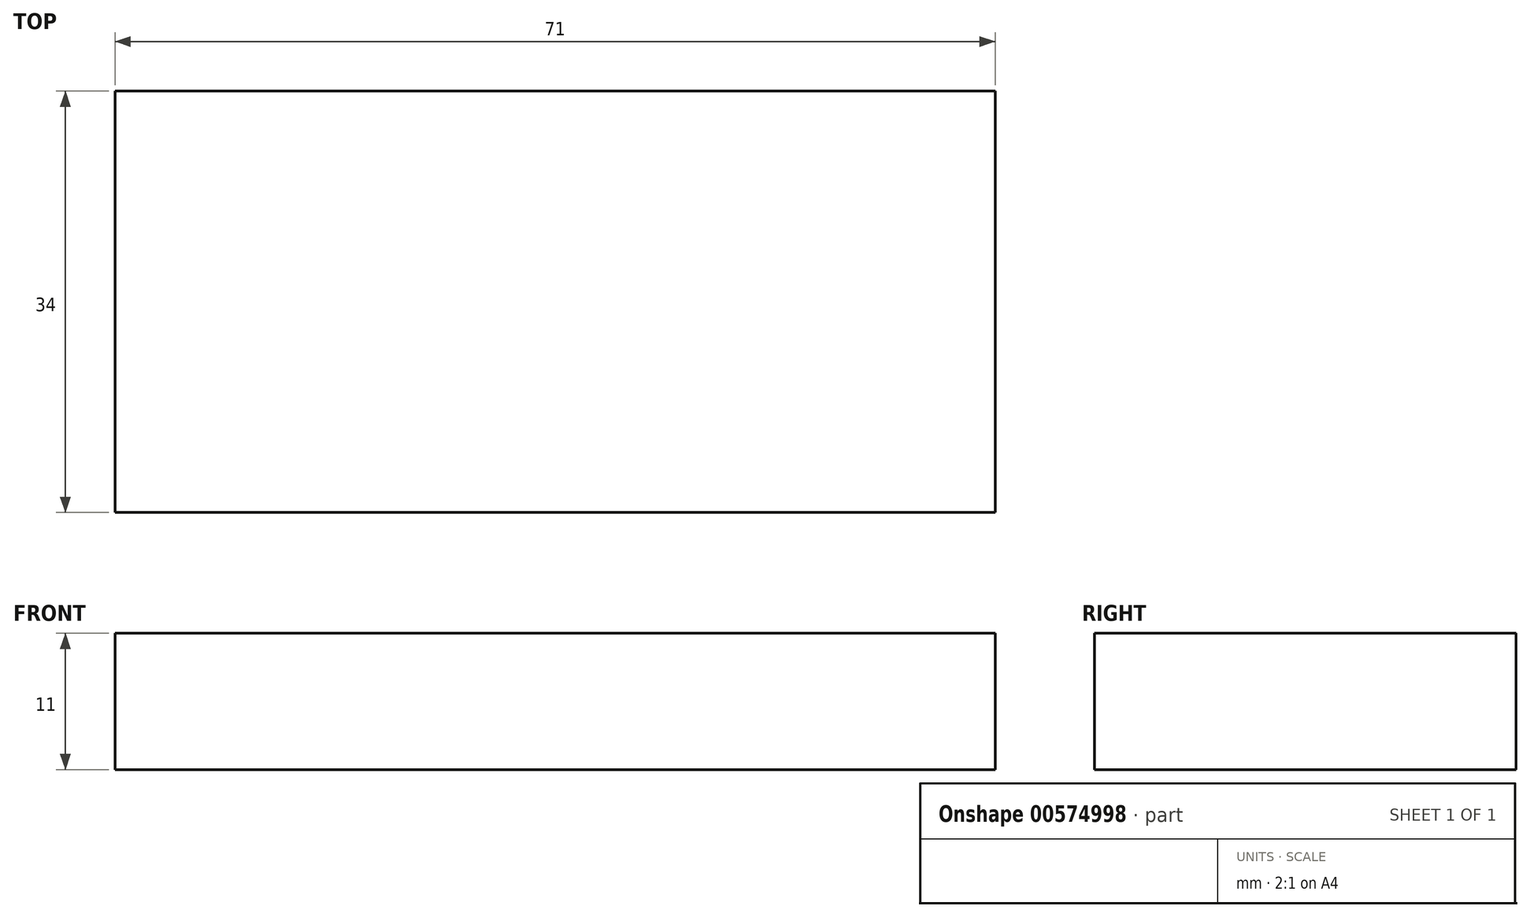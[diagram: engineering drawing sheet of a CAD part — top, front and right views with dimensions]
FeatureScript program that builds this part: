
annotation { "Feature Type Name" : "Feature", "Feature Type Description" : "" }
export const myFeature = defineFeature(function(context is Context, id is Id, definition is map)
    precondition{}
    {
        {
            var Q0;
            Q0=qCreatedBy(makeId("Top.planeOp"),FACE);
            var sketch = newSketch(context, id + "F0", { "sketchPlane" : qUnion([Q0])});
            skLineSegment(sketch, "E0.bottom", {"start": v(-35.5, 17) * mm, "end": v(35.5, 17) * mm});
            skLineSegment(sketch, "E0.top", {"start": v(-35.5, -17) * mm, "end": v(35.5, -17) * mm});
            skLineSegment(sketch, "E0.left", {"start": v(-35.5, 17) * mm, "end": v(-35.5, -17) * mm});
            skLineSegment(sketch, "E0.right", {"start": v(35.5, 17) * mm, "end": v(35.5, -17) * mm});
            skPoint(sketch, "E0.middle", {"position": v(0, 0) * mm});
            skSolve(sketch);
        }
        {
            var Q0;
            Q0 = qSketchRegion(id + "F0", true);
            extrude(context, id + "F1", {"entities" : qUnion([Q0]), "depth" : (11 / 2) * mm, "offsetDistance" : 25 * mm, "hasSecondDirection" : true, "secondDirectionOppositeDirection" : true, "secondDirectionDepth" : (11 / 2) * mm});
        }
    });
